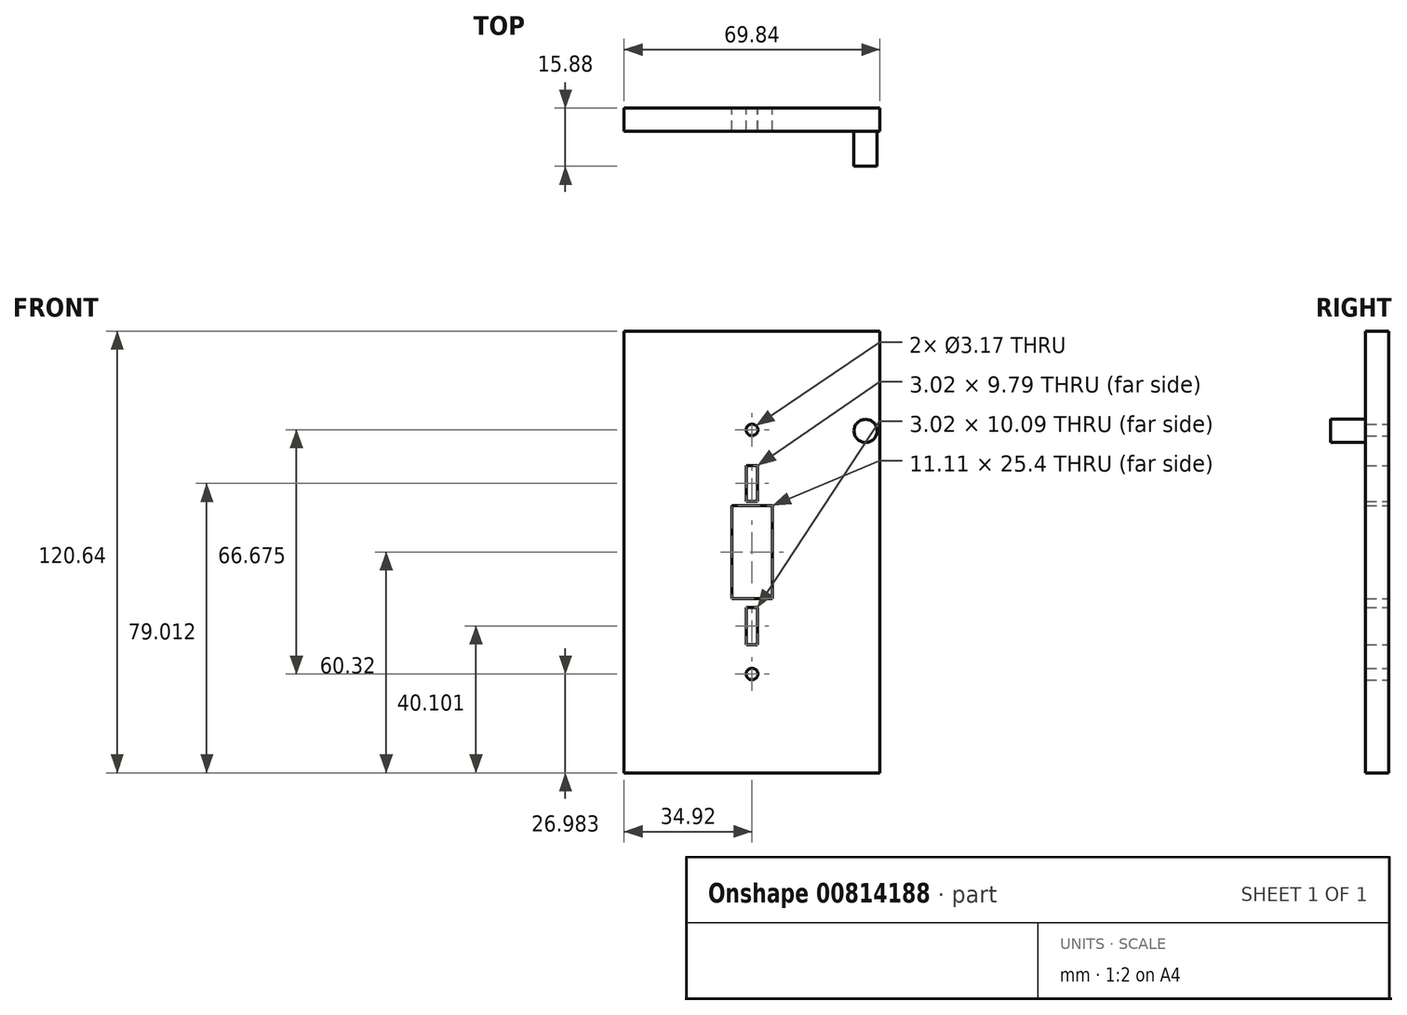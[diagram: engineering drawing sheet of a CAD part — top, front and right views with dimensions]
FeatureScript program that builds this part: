
annotation { "Feature Type Name" : "Feature", "Feature Type Description" : "" }
export const myFeature = defineFeature(function(context is Context, id is Id, definition is map)
    precondition{}
    {
        {
            var Q0;
            Q0=qCreatedBy(makeId("Front.planeOp"),FACE);
            var sketch = newSketch(context, id + "F0", { "sketchPlane" : qUnion([Q0])});
            skLineSegment(sketch, "E0.bottom", {"start": v(34.92, 60.33) * mm, "end": v(-34.92, 60.33) * mm});
            skLineSegment(sketch, "E0.top", {"start": v(34.92, -60.33) * mm, "end": v(-34.92, -60.33) * mm});
            skLineSegment(sketch, "E0.left", {"start": v(34.92, 60.33) * mm, "end": v(34.92, -60.33) * mm});
            skLineSegment(sketch, "E0.right", {"start": v(-34.92, 60.33) * mm, "end": v(-34.92, -60.33) * mm});
            skPoint(sketch, "E0.middle", {"position": v(0, 0) * mm});
            skLineSegment(sketch, "E1.bottom", {"start": v(5.56, 12.7) * mm, "end": v(-5.56, 12.7) * mm});
            skLineSegment(sketch, "E1.top", {"start": v(5.56, -12.7) * mm, "end": v(-5.56, -12.7) * mm});
            skLineSegment(sketch, "E1.left", {"start": v(5.56, 12.7) * mm, "end": v(5.56, -12.7) * mm});
            skLineSegment(sketch, "E1.right", {"start": v(-5.56, 12.7) * mm, "end": v(-5.56, -12.7) * mm});
            skCircle(sketch, "E2", {"center": v(0, -33.34) * mm, "radius": 1.59 * mm});
            skCircle(sketch, "E3.MirrorC", {"center": v(0, 33.34) * mm, "radius": 1.59 * mm});
            skCircle(sketch, "E4", {"center": v(31, 33.05) * mm, "radius": 3.18 * mm});
            skLineSegment(sketch, "E5", {"start": v(-1.51, 12.7) * mm, "end": v(-1.51, 23.59) * mm});
            skLineSegment(sketch, "E6", {"start": v(1.51, 12.7) * mm, "end": v(1.51, 23.59) * mm});
            skLineSegment(sketch, "E7", {"start": v(-1.51, 13.8) * mm, "end": v(1.51, 13.8) * mm});
            skLineSegment(sketch, "E8", {"start": v(1.51, 23.59) * mm, "end": v(-1.51, 23.59) * mm});
            skLineSegment(sketch, "E9.MirrorCS", {"start": v(-1.51, -15.17) * mm, "end": v(1.51, -15.17) * mm});
            skLineSegment(sketch, "E10", {"start": v(-1.51, -12.7) * mm, "end": v(-1.51, -25.27) * mm});
            skLineSegment(sketch, "E11", {"start": v(1.51, -12.7) * mm, "end": v(1.51, -25.27) * mm});
            skPoint(sketch, "E12.endSnap0", {"position": v(1.51, -18.98) * mm});
            skLineSegment(sketch, "E13.MirrorCS", {"start": v(1.51, -25.27) * mm, "end": v(-1.51, -25.27) * mm});
            skSolve(sketch);
        }
        {
            var Q0;
            Q0=makeQuery(id+"F0.imprint","IMPRINT",FACE,{"disambiguationData":[TD([[makeQuery(id+"F0.imprint","IMPRINT",EDGE,{"derivedFrom":sQuery(id+"F0.wireOp",EDGE,"E4")}),1.0]])]});
            extrude(context, id + "F1", {"entities" : qUnion([Q0]), "depth" : 12.7 * mm, "offsetDistance" : 25.4 * mm});
        }
        {
            var Q0;
            Q0=makeQuery(id+"F0.imprint","IMPRINT",FACE,{"disambiguationData":[TD([[makeQuery(id+"F0.imprint","IMPRINT",EDGE,{"derivedFrom":sQuery(id+"F0.wireOp",EDGE,"E0.bottom")}),1.0]])]});
            var Q1;
            {var subQ5=sQuery(id+"F0.wireOp",EDGE,"bVnIY8FM-bTXH-YMS7-tbxk-f2d9sLIcQtJs");Q1=makeQuery(id+"F0.imprint","IMPRINT",FACE,{"disambiguationData":[TD([[makeQuery(id+"F0.imprint","IMPRINT",EDGE,{"derivedFrom":subQ5}),-1.0]])]});}
            var Q2;
            {var subQ5=sQuery(id+"F0.wireOp",EDGE,"E7");Q2=makeQuery(id+"F0.imprint","IMPRINT",FACE,{"disambiguationData":[TD([[makeQuery(id+"F0.imprint","IMPRINT",EDGE,{"derivedFrom":subQ5}),-1.0]])]});}
            var Q3;
            Q3=makeQuery(id+"F0.imprint","IMPRINT",FACE,{"disambiguationData":[TD([[makeQuery(id+"F0.imprint","IMPRINT",EDGE,{"derivedFrom":sQuery(id+"F0.wireOp",EDGE,"E4")}),1.0]])]});
            var Q4;
            {var subQ5=sQuery(id+"F0.wireOp",EDGE,"E9.MirrorCS");Q4=makeQuery(id+"F0.imprint","IMPRINT",FACE,{"disambiguationData":[TD([[makeQuery(id+"F0.imprint","IMPRINT",EDGE,{"derivedFrom":subQ5}),1.0]])]});}
            extrude(context, id + "F2", {"entities" : qUnion([Q0, Q1, Q2, Q3, Q4]), "operationType" : NewBodyOperationType.ADD, "endBound" : BoundingType.SYMMETRIC, "depth" : 6.35 * mm, "offsetDistance" : 25.4 * mm});
        }
    });
